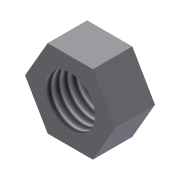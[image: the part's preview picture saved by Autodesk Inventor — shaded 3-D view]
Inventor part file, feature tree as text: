
AUTODESK INVENTOR PART (.ipt)
format: ipt  version: 2016 (Build 200138000, 138)  size: 84,992 bytes
history: native  units: mm
features: extrude x1, thread x1, sketch x1
ambient origin geometry x8: Origin, YZ Plane, XZ Plane, XY Plane, X Axis, Y Axis, Z Axis, Center Point
bodies: Solid1 (feature_tree)
feature tree (3):
  extrude  "Extrusion1"  Depth=2.4mm TaperAngle=0.0deg
  thread  "Thread1"  [1 undecoded]
  sketch  "Sketch1"  dims[d19=3.0mm d20=2.4mm d21=0.0mm d22=10.0mm d23=0.0mm]
note: 1 required parameter value undecoded (feature->parameter linkage not recoverable at this tier; creation-order binding heuristic only, values carry confidence <= 0.55)
